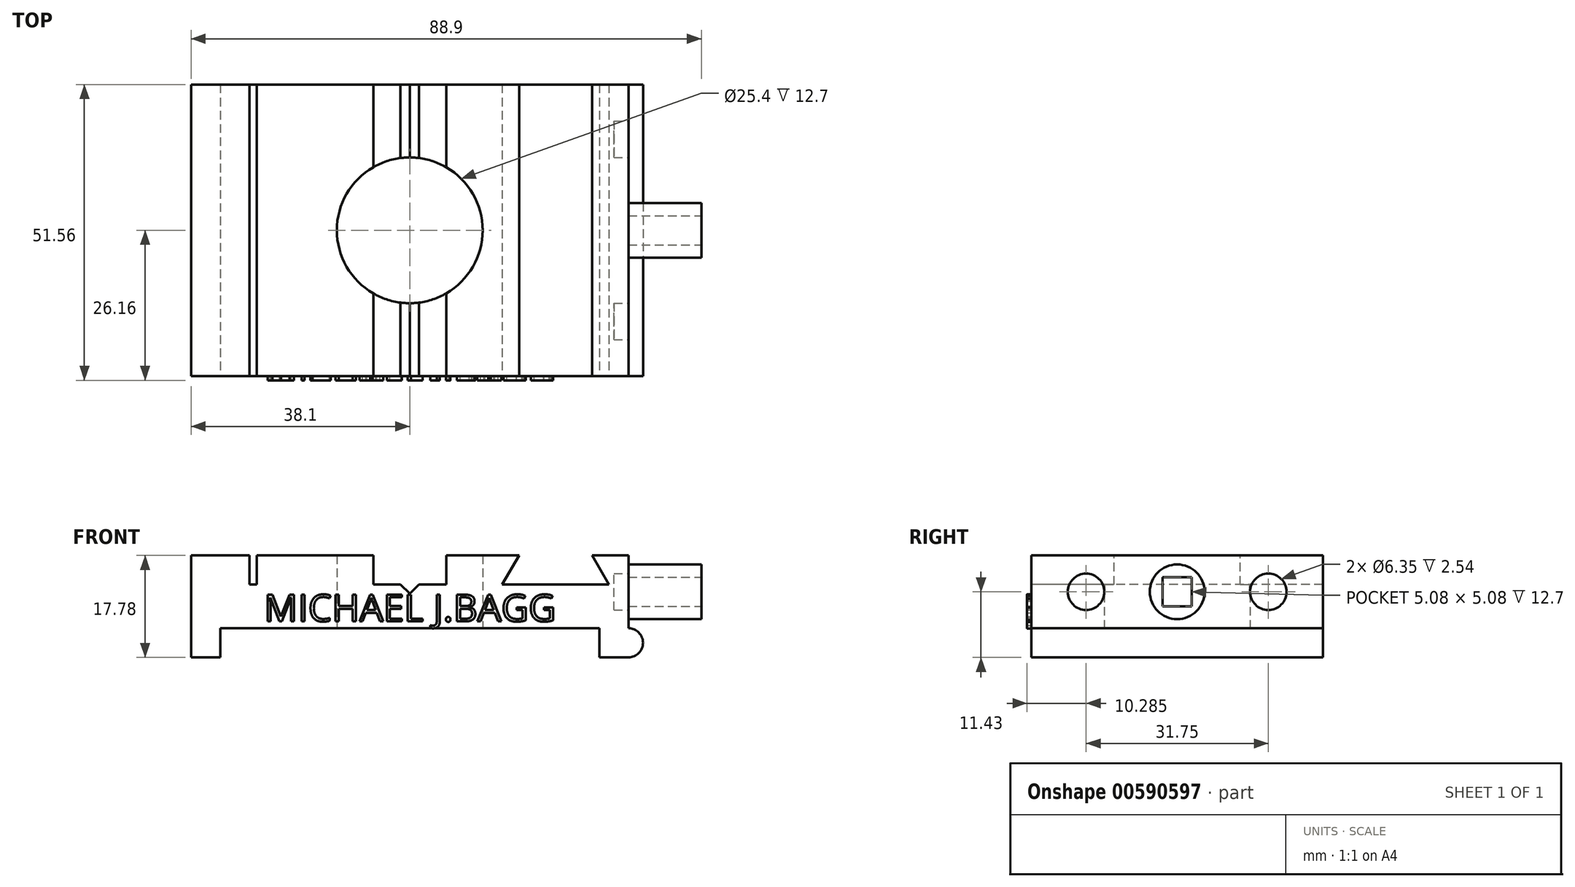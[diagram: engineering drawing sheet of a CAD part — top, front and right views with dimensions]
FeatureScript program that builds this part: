
annotation { "Feature Type Name" : "Feature", "Feature Type Description" : "" }
export const myFeature = defineFeature(function(context is Context, id is Id, definition is map)
    precondition{}
    {
        {
            var Q0;
            Q0=qCreatedBy(makeId("Top.planeOp"),FACE);
            var sketch = newSketch(context, id + "F0", { "sketchPlane" : qUnion([Q0])});
            skLineSegment(sketch, "E0.bottom", {"start": v(-38.1, 25.4) * mm, "end": v(38.1, 25.4) * mm});
            skLineSegment(sketch, "E0.top", {"start": v(-38.1, -25.4) * mm, "end": v(38.1, -25.4) * mm});
            skLineSegment(sketch, "E0.left", {"start": v(-38.1, 25.4) * mm, "end": v(-38.1, -25.4) * mm});
            skLineSegment(sketch, "E0.right", {"start": v(38.1, 25.4) * mm, "end": v(38.1, -25.4) * mm});
            skPoint(sketch, "E0.middle", {"position": v(0, 0) * mm});
            skCircle(sketch, "E1", {"center": v(0, 0) * mm, "radius": 12.7 * mm});
            skSolve(sketch);
        }
        {
            var Q0;
            Q0 = qSketchRegion(id + "F0", true);
            extrude(context, id + "F1", {"entities" : qUnion([Q0]), "depth" : 12.7 * mm, "offsetDistance" : 25 * mm});
        }
        {
            var Q0;
            Q0=makeQuery(id+"F1.opExtrude","CAP_FACE",FACE,{"disambiguationData":[OSD([sQuery(id+"F0.wireOp",EDGE,"E0.bottom"),sQuery(id+"F0.wireOp",EDGE,"E0.top"),sQuery(id+"F0.wireOp",EDGE,"E0.left"),sQuery(id+"F0.wireOp",EDGE,"E0.right"),sQuery(id+"F0.wireOp",EDGE,"E1")])],"isStart":false});
            var sketch = newSketch(context, id + "F2", { "sketchPlane" : qUnion([Q0])});
            skLineSegment(sketch, "E2.bottom", {"start": v(-27.94, 25.4) * mm, "end": v(-26.67, 25.4) * mm});
            skLineSegment(sketch, "E2.top", {"start": v(-27.94, -25.4) * mm, "end": v(-26.67, -25.4) * mm});
            skLineSegment(sketch, "E2.left", {"start": v(-27.94, 25.4) * mm, "end": v(-27.94, -25.4) * mm});
            skLineSegment(sketch, "E2.right", {"start": v(-26.67, 25.4) * mm, "end": v(-26.67, -25.4) * mm});
            skLineSegment(sketch, "E3", {"start": v(-6.35, 25.4) * mm, "end": v(-6.35, -25.4) * mm});
            skLineSegment(sketch, "E4", {"start": v(-6.35, 25.4) * mm, "end": v(6.35, 25.4) * mm});
            skLineSegment(sketch, "E5", {"start": v(6.35, 25.4) * mm, "end": v(6.35, -25.4) * mm});
            skLineSegment(sketch, "E6", {"start": v(6.35, -25.4) * mm, "end": v(-6.35, -25.4) * mm});
            skPoint(sketch, "E7", {"position": v(0, 0) * mm});
            skLineSegment(sketch, "E8", {"start": v(0, 25.4) * mm, "end": v(0, -25.4) * mm, "construction": true});
            skSolve(sketch);
        }
        {
            var Q0;
            Q0=makeQuery(id+"F2.imprint","IMPRINT",FACE,{"disambiguationData":[TD([[makeQuery(id+"F2.imprint","IMPRINT",EDGE,{"derivedFrom":sQuery(id+"F2.wireOp",EDGE,"E2.bottom")}),-1.0]])]});
            var Q1;
            {var subQ0=sQuery(id+"F2.wireOp",EDGE,"E6");Q1=makeQuery(id+"F2.imprint","IMPRINT",FACE,{"disambiguationData":[TD([[makeQuery(id+"F2.imprint","IMPRINT",EDGE,{"derivedFrom":subQ0}),1.0]])]});}
            var Q2;
            {var subQ0=sQuery(id+"F2.wireOp",EDGE,"E4");Q2=makeQuery(id+"F2.imprint","IMPRINT",FACE,{"disambiguationData":[TD([[makeQuery(id+"F2.imprint","IMPRINT",EDGE,{"derivedFrom":subQ0}),-1.0]])]});}
            extrude(context, id + "F3", {"entities" : qUnion([Q0, Q1, Q2]), "operationType" : NewBodyOperationType.REMOVE, "oppositeDirection" : true, "depth" : 5.08 * mm, "offsetDistance" : 25.4 * mm});
        }
        {
            var Q0;
            Q0=makeQuery(id+"F1.opExtrude","SWEPT_FACE",FACE,{"disambiguationData":[OSD([sQuery(id+"F0.wireOp",EDGE,"E0.top")])]});
            var sketch = newSketch(context, id + "F4", { "sketchPlane" : qUnion([Q0])});
            skLineSegment(sketch, "E9", {"start": v(19.05, 12.7) * mm, "end": v(16.12, 7.62) * mm});
            skLineSegment(sketch, "E10", {"start": v(16.12, 7.62) * mm, "end": v(34.68, 7.62) * mm});
            skLineSegment(sketch, "E11", {"start": v(34.68, 7.62) * mm, "end": v(31.75, 12.7) * mm});
            skLineSegment(sketch, "E12", {"start": v(31.75, 12.7) * mm, "end": v(19.05, 12.7) * mm});
            skLineSegment(sketch, "E13", {"start": v(25.4, 7.62) * mm, "end": v(25.4, 12.7) * mm, "construction": true});
            skSolve(sketch);
        }
        {
            var Q0;
            Q0=makeQuery(id+"F4.imprint","IMPRINT",FACE,{"disambiguationData":[TD([[makeQuery(id+"F4.imprint","IMPRINT",EDGE,{"derivedFrom":sQuery(id+"F4.wireOp",EDGE,"E9")}),1.0]])]});
            extrude(context, id + "F5", {"entities" : qUnion([Q0]), "operationType" : NewBodyOperationType.REMOVE, "endBound" : BoundingType.THROUGH_ALL, "oppositeDirection" : true, "depth" : 25.4 * mm, "offsetDistance" : 25.4 * mm});
        }
        {
            var Q0;
            Q0=makeQuery(id+"F1.opExtrude","SWEPT_FACE",FACE,{"disambiguationData":[OSD([sQuery(id+"F0.wireOp",EDGE,"E0.right")])]});
            var sketch = newSketch(context, id + "F6", { "sketchPlane" : qUnion([Q0])});
            skCircle(sketch, "E14", {"center": v(0, 6.35) * mm, "radius": 4.76 * mm});
            skPoint(sketch, "E14.centerSnap0", {"position": v(-25.4, 6.35) * mm});
            skPoint(sketch, "E14.centerSnap1", {"position": v(0, 12.7) * mm});
            skSolve(sketch);
        }
        {
            var Q0;
            Q0 = qSketchRegion(id + "F6", true);
            extrude(context, id + "F7", {"entities" : qUnion([Q0]), "operationType" : NewBodyOperationType.ADD, "depth" : 12.7 * mm, "offsetDistance" : 25.4 * mm});
        }
        {
            var Q0;
            Q0=makeQuery(id+"F1.opExtrude","SWEPT_FACE",FACE,{"disambiguationData":[OSD([sQuery(id+"F0.wireOp",EDGE,"E0.top")])]});
            var sketch = newSketch(context, id + "F8", { "sketchPlane" : qUnion([Q0])});
            skLineSegment(sketch, "E15.bottom", {"start": v(-38.1, 0) * mm, "end": v(-33.02, 0) * mm});
            skLineSegment(sketch, "E15.top", {"start": v(-38.1, -5.08) * mm, "end": v(-33.02, -5.08) * mm});
            skLineSegment(sketch, "E15.left", {"start": v(-38.1, 0) * mm, "end": v(-38.1, -5.08) * mm});
            skLineSegment(sketch, "E15.right", {"start": v(-33.02, 0) * mm, "end": v(-33.02, -5.08) * mm});
            skLineSegment(sketch, "E16.bottom", {"start": v(38.1, 0) * mm, "end": v(33.02, 0) * mm});
            skLineSegment(sketch, "E16.top", {"start": v(38.1, -5.08) * mm, "end": v(33.02, -5.08) * mm});
            skLineSegment(sketch, "E16.left", {"start": v(38.1, 0) * mm, "end": v(38.1, -5.08) * mm});
            skLineSegment(sketch, "E16.right", {"start": v(33.02, 0) * mm, "end": v(33.02, -5.08) * mm});
            skSolve(sketch);
        }
        {
            var Q0;
            Q0 = qSketchRegion(id + "F8", true);
            var Q1;
            Q1=makeQuery(id+"F1.opExtrude","SWEPT_FACE",FACE,{"disambiguationData":[OSD([sQuery(id+"F0.wireOp",EDGE,"E0.bottom")])]});
            extrude(context, id + "F9", {"entities" : qUnion([Q0]), "operationType" : NewBodyOperationType.ADD, "endBound" : BoundingType.UP_TO_SURFACE, "oppositeDirection" : true, "depth" : 25.4 * mm, "endBoundEntityFace" : qUnion([Q1]), "offsetDistance" : 25.4 * mm});
        }
        {
            var Q0;
            Q0=makeQuery(id+"F7.opExtrude","CAP_FACE",FACE,{"disambiguationData":[OSD([sQuery(id+"F6.wireOp",EDGE,"E14")])],"isStart":false});
            var sketch = newSketch(context, id + "F10", { "sketchPlane" : qUnion([Q0])});
            skPoint(sketch, "E17", {"position": v(0, 6.35) * mm});
            skLineSegment(sketch, "E18.bottom", {"start": v(-2.54, 8.9) * mm, "end": v(2.54, 8.9) * mm});
            skLineSegment(sketch, "E18.top", {"start": v(-2.54, 3.81) * mm, "end": v(2.54, 3.81) * mm});
            skLineSegment(sketch, "E18.left", {"start": v(-2.54, 8.9) * mm, "end": v(-2.54, 3.81) * mm});
            skLineSegment(sketch, "E18.right", {"start": v(2.54, 8.9) * mm, "end": v(2.54, 3.81) * mm});
            skSolve(sketch);
        }
        {
            var Q0;
            Q0 = qSketchRegion(id + "F10", true);
            extrude(context, id + "F11", {"entities" : qUnion([Q0]), "operationType" : NewBodyOperationType.REMOVE, "oppositeDirection" : true, "depth" : 12.7 * mm, "offsetDistance" : 25.4 * mm});
        }
        {
            var Q0;
            Q0=makeQuery(id+"F9.boolean.opBoolean","MERGE",FACE,{"derivedFrom":[makeQuery(id+"F1.opExtrude","SWEPT_FACE",FACE,{"disambiguationData":[OSD([sQuery(id+"F0.wireOp",EDGE,"E0.top")])]}),makeQuery(id+"F9.opExtrude","CAP_FACE",FACE,{"disambiguationData":[OSD([sQuery(id+"F8.wireOp",EDGE,"E15.bottom"),sQuery(id+"F8.wireOp",EDGE,"E15.top"),sQuery(id+"F8.wireOp",EDGE,"E15.left"),sQuery(id+"F8.wireOp",EDGE,"E15.right")])],"isStart":true}),makeQuery(id+"F9.opExtrude","CAP_FACE",FACE,{"disambiguationData":[OSD([sQuery(id+"F8.wireOp",EDGE,"E16.bottom"),sQuery(id+"F8.wireOp",EDGE,"E16.top"),sQuery(id+"F8.wireOp",EDGE,"E16.left"),sQuery(id+"F8.wireOp",EDGE,"E16.right")])],"isStart":true})]});
            var sketch = newSketch(context, id + "F12", { "sketchPlane" : qUnion([Q0])});
            skArc(sketch, "E19", {"start": v(38.1, -5.08) * mm, "mid": v(40.64, -2.54) * mm, "end": v(38.1, 0) * mm});
            skPoint(sketch, "E19.centerSnap0", {"position": v(33.02, -2.54) * mm});
            skLineSegment(sketch, "E20", {"start": v(38.1, 0) * mm, "end": v(38.1, -5.08) * mm});
            skSolve(sketch);
        }
        {
            var Q0;
            Q0=makeQuery(id+"F12.imprint","IMPRINT",FACE,{"disambiguationData":[TD([[makeQuery(id+"F12.imprint","IMPRINT",EDGE,{"derivedFrom":sQuery(id+"F12.wireOp",EDGE,"E19")}),1.0]])]});
            var Q1;
            {var subQ0=sQuery(id+"F0.wireOp",EDGE,"E0.bottom");Q1=makeQuery(id+"F9.boolean.opBoolean","MERGE",FACE,{"derivedFrom":[makeQuery(id+"F1.opExtrude","SWEPT_FACE",FACE,{"disambiguationData":[OSD([subQ0])]}),makeQuery(id+"F9.opExtrude","CAP_FACE",FACE,{"disambiguationData":[OSD([subQ0]),OD(0.0)],"isStart":false}),makeQuery(id+"F9.opExtrude","CAP_FACE",FACE,{"disambiguationData":[OSD([subQ0]),OD(1.0)],"isStart":false})]});}
            extrude(context, id + "F13", {"entities" : qUnion([Q0]), "operationType" : NewBodyOperationType.ADD, "endBound" : BoundingType.UP_TO_SURFACE, "oppositeDirection" : true, "depth" : 25.4 * mm, "endBoundEntityFace" : qUnion([Q1]), "offsetDistance" : 25.4 * mm});
        }
        {
            var Q0;
            Q0=makeQuery(id+"F9.boolean.opBoolean","MERGE",FACE,{"derivedFrom":[makeQuery(id+"F1.opExtrude","SWEPT_FACE",FACE,{"disambiguationData":[OSD([sQuery(id+"F0.wireOp",EDGE,"E0.right")])]}),makeQuery(id+"F9.opExtrude","SWEPT_FACE",FACE,{"disambiguationData":[OSD([sQuery(id+"F8.wireOp",EDGE,"E16.left")])]})]});
            var sketch = newSketch(context, id + "F14", { "sketchPlane" : qUnion([Q0])});
            skPoint(sketch, "E21", {"position": v(0, 6.35) * mm});
            skLineSegment(sketch, "E22", {"start": v(0, 6.35) * mm, "end": v(-15.87, 6.35) * mm, "construction": true});
            skLineSegment(sketch, "E23", {"start": v(0, 6.35) * mm, "end": v(15.88, 6.35) * mm, "construction": true});
            skCircle(sketch, "E24", {"center": v(-15.87, 6.35) * mm, "radius": 3.18 * mm});
            skCircle(sketch, "E25", {"center": v(15.88, 6.35) * mm, "radius": 3.18 * mm});
            skSolve(sketch);
        }
        {
            var Q0;
            Q0 = qSketchRegion(id + "F14", true);
            extrude(context, id + "F15", {"entities" : qUnion([Q0]), "operationType" : NewBodyOperationType.REMOVE, "oppositeDirection" : true, "depth" : 2.54 * mm, "offsetDistance" : 25.4 * mm});
        }
        {
            var Q0;
            {var subQ0=sQuery(id+"F12.wireOp",EDGE,"E20");var subQ1=sQuery(id+"F12.wireOp",EDGE,"E19");Q0=makeQuery(id+"FJm9RPYZez87fcW_1.1.F13.boolean.opBoolean","MERGE",FACE,{"derivedFrom":[makeQuery(id+"F13.boolean.opBoolean","MERGE",FACE,{"derivedFrom":[makeQuery(id+"F9.boolean.opBoolean","MERGE",FACE,{"derivedFrom":[makeQuery(id+"F1.opExtrude","SWEPT_FACE",FACE,{"disambiguationData":[OSD([sQuery(id+"F0.wireOp",EDGE,"E0.top")])]}),makeQuery(id+"F9.opExtrude","CAP_FACE",FACE,{"disambiguationData":[OSD([sQuery(id+"F8.wireOp",EDGE,"E15.bottom"),sQuery(id+"F8.wireOp",EDGE,"E15.top"),sQuery(id+"F8.wireOp",EDGE,"E15.left"),sQuery(id+"F8.wireOp",EDGE,"E15.right")])],"isStart":true}),makeQuery(id+"F9.opExtrude","CAP_FACE",FACE,{"disambiguationData":[OSD([sQuery(id+"F8.wireOp",EDGE,"E16.bottom"),sQuery(id+"F8.wireOp",EDGE,"E16.top"),sQuery(id+"F8.wireOp",EDGE,"E16.left"),sQuery(id+"F8.wireOp",EDGE,"E16.right")])],"isStart":true})]}),makeQuery(id+"F13.opExtrude","CAP_FACE",FACE,{"disambiguationData":[OSD([subQ1,subQ0])],"isStart":true})]}),makeQuery(id+"FJm9RPYZez87fcW_1.1.F13.opExtrude","CAP_FACE",FACE,{"disambiguationData":[OSD([subQ1,subQ0])],"isStart":true})]});}
            var sketch = newSketch(context, id + "F16", { "sketchPlane" : qUnion([Q0])});
            skLineSegment(sketch, "E26", {"start": v(0, 7.62) * mm, "end": v(0, 0) * mm, "construction": true});
            skLineSegment(sketch, "E27", {"start": v(-1.6, 7.62) * mm, "end": v(0, 6.02) * mm});
            skLineSegment(sketch, "E28", {"start": v(0, 6.02) * mm, "end": v(1.6, 7.62) * mm});
            skLineSegment(sketch, "E29", {"start": v(1.6, 7.62) * mm, "end": v(-1.6, 7.62) * mm});
            skSolve(sketch);
        }
        {
            var Q0;
            Q0 = qSketchRegion(id + "F16", true);
            var Q1;
            {var subQ0=sQuery(id+"F0.wireOp",EDGE,"E0.bottom");Q1=makeQuery(id+"FJm9RPYZez87fcW_1.1.F13.boolean.opBoolean","MERGE",FACE,{"derivedFrom":[makeQuery(id+"F13.boolean.opBoolean","MERGE",FACE,{"derivedFrom":[makeQuery(id+"F9.boolean.opBoolean","MERGE",FACE,{"derivedFrom":[makeQuery(id+"F1.opExtrude","SWEPT_FACE",FACE,{"disambiguationData":[OSD([subQ0])]}),makeQuery(id+"F9.opExtrude","CAP_FACE",FACE,{"disambiguationData":[OSD([subQ0]),OD(0.0)],"isStart":false}),makeQuery(id+"F9.opExtrude","CAP_FACE",FACE,{"disambiguationData":[OSD([subQ0]),OD(1.0)],"isStart":false})]}),makeQuery(id+"F13.opExtrude","CAP_FACE",FACE,{"disambiguationData":[OSD([subQ0])],"isStart":false})]}),makeQuery(id+"FJm9RPYZez87fcW_1.1.F13.opExtrude","CAP_FACE",FACE,{"disambiguationData":[OSD([subQ0])],"isStart":false})]});}
            extrude(context, id + "F17", {"entities" : qUnion([Q0]), "operationType" : NewBodyOperationType.REMOVE, "endBound" : BoundingType.UP_TO_SURFACE, "oppositeDirection" : true, "depth" : 25.4 * mm, "endBoundEntityFace" : qUnion([Q1]), "offsetDistance" : 25.4 * mm});
        }
        {
            var Q0;
            {var subQ0=sQuery(id+"F12.wireOp",EDGE,"E20");var subQ1=sQuery(id+"F12.wireOp",EDGE,"E19");Q0=makeQuery(id+"FJm9RPYZez87fcW_1.1.F13.boolean.opBoolean","MERGE",FACE,{"derivedFrom":[makeQuery(id+"F13.boolean.opBoolean","MERGE",FACE,{"derivedFrom":[makeQuery(id+"F9.boolean.opBoolean","MERGE",FACE,{"derivedFrom":[makeQuery(id+"F1.opExtrude","SWEPT_FACE",FACE,{"disambiguationData":[OSD([sQuery(id+"F0.wireOp",EDGE,"E0.top")])]}),makeQuery(id+"F9.opExtrude","CAP_FACE",FACE,{"disambiguationData":[OSD([sQuery(id+"F8.wireOp",EDGE,"E15.bottom"),sQuery(id+"F8.wireOp",EDGE,"E15.top"),sQuery(id+"F8.wireOp",EDGE,"E15.left"),sQuery(id+"F8.wireOp",EDGE,"E15.right")])],"isStart":true}),makeQuery(id+"F9.opExtrude","CAP_FACE",FACE,{"disambiguationData":[OSD([sQuery(id+"F8.wireOp",EDGE,"E16.bottom"),sQuery(id+"F8.wireOp",EDGE,"E16.top"),sQuery(id+"F8.wireOp",EDGE,"E16.left"),sQuery(id+"F8.wireOp",EDGE,"E16.right")])],"isStart":true})]}),makeQuery(id+"F13.opExtrude","CAP_FACE",FACE,{"disambiguationData":[OSD([subQ1,subQ0])],"isStart":true})]}),makeQuery(id+"FJm9RPYZez87fcW_1.1.F13.opExtrude","CAP_FACE",FACE,{"disambiguationData":[OSD([subQ1,subQ0])],"isStart":true})]});}
            var sketch = newSketch(context, id + "F18", { "sketchPlane" : qUnion([Q0])});
            skLineSegment(sketch, "E30", {"start": v(0, 6.02) * mm, "end": v(0, 0) * mm, "construction": true});
            skPoint(sketch, "E31", {"position": v(0, 3) * mm});
            skText(sketch, "E32", { "text": "MICHAEL J.BAGG", "fontName": "OpenSans-Regular.ttf"});
            const initialGuessF18  = {"E32": [-0.0254, 0.0012, 1, 0, 0.0047]};
            skSetInitialGuess(sketch, initialGuessF18);
            skSolve(sketch);
        }
        {
            var Q0;
            Q0 = qSketchRegion(id + "F18", true);
            extrude(context, id + "F19", {"entities" : qUnion([Q0]), "operationType" : NewBodyOperationType.ADD, "depth" : 0.76 * mm, "offsetDistance" : 25.4 * mm});
        }
    });
